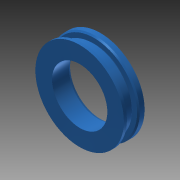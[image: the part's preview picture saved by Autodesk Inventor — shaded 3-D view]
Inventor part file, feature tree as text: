
AUTODESK INVENTOR PART (.ipt)
format: ipt  version: 2013 (Build 170138000, 138)  size: 139,264 bytes
history: native  units: mm
features: revolve x1, sketch x1
ambient origin geometry x8: Origin, YZ Plane, XZ Plane, XY Plane, X Axis, Y Axis, Z Axis, Center Point
bodies: Solid1 (feature_tree)
feature tree (2):
  revolve  "Revolution1"  [1 undecoded]
  sketch  "Sketch1"  dims[d6=8.0mm d7=11.1mm d10=90.0deg d12=1.0mm d13=6.0mm d14=6.0mm d17=3.2mm d18=1.9mm d19=135.0deg d24=0.5mm d25=0.5mm d27=0.6mm d28=1.0mm d29=0.4mm d30=0.4mm]
note: 1 required parameter value undecoded (feature->parameter linkage not recoverable at this tier; creation-order binding heuristic only, values carry confidence <= 0.55)
